# Revit family: QF_BOURGEAT_2_silos_fixe_couvercle_carre
name_source: partatom
category: Equipement spécialisé
revit_build: Autodesk Revit 2015 (Build: 20140606_1530(x64)
units: mm (PartAtom-declared; Revit-internal decimal feet)

## types (3) — shared parameters
Fabricant = BOURGEAT
Fréquence = 50 Hz
Hauteur hors tout = 900 mm  [stored 2.95276 ft]
Phase = 2
Spécification du Fabricant = SILOS FIXE
Tension = 230 V
URL catalogue = http://www.bourgeat.fr

## per-type parameters (varying)
| type | Charge max | Indice de protection | Intensité nominale | Longueur hors tout | Modèle | Poids net à vide | Profondeur hors tout | Puissance électrique  |
| chauffant_non_ventile_assiettes_200/260 | 140.00 kg | 25 | 4 A | 442 mm  [stored 1.45013 ft] | 777426+777438 | 37.00 kg | 898 mm  [stored 2.94619 ft] | 950 W |
| chauffant_ventile_assiettes_200/260 | 140.00 kg | 25 | 4 A | 442 mm  [stored 1.45013 ft] | 777446+777438 | 37.00 kg | 892 mm | 950 W |
| chauffant_non_ventile_assiettes200/285 | 160.00 kg | 21 | 6 A | 510 mm  [stored 1.67323 ft] | 777406+777437 | 55.00 kg | 990 mm  [stored 3.24803 ft] | 1400 W |

note: [stored X ft] marks values corroborated as IEEE doubles in the binary element streams (Revit-internal decimal feet)
